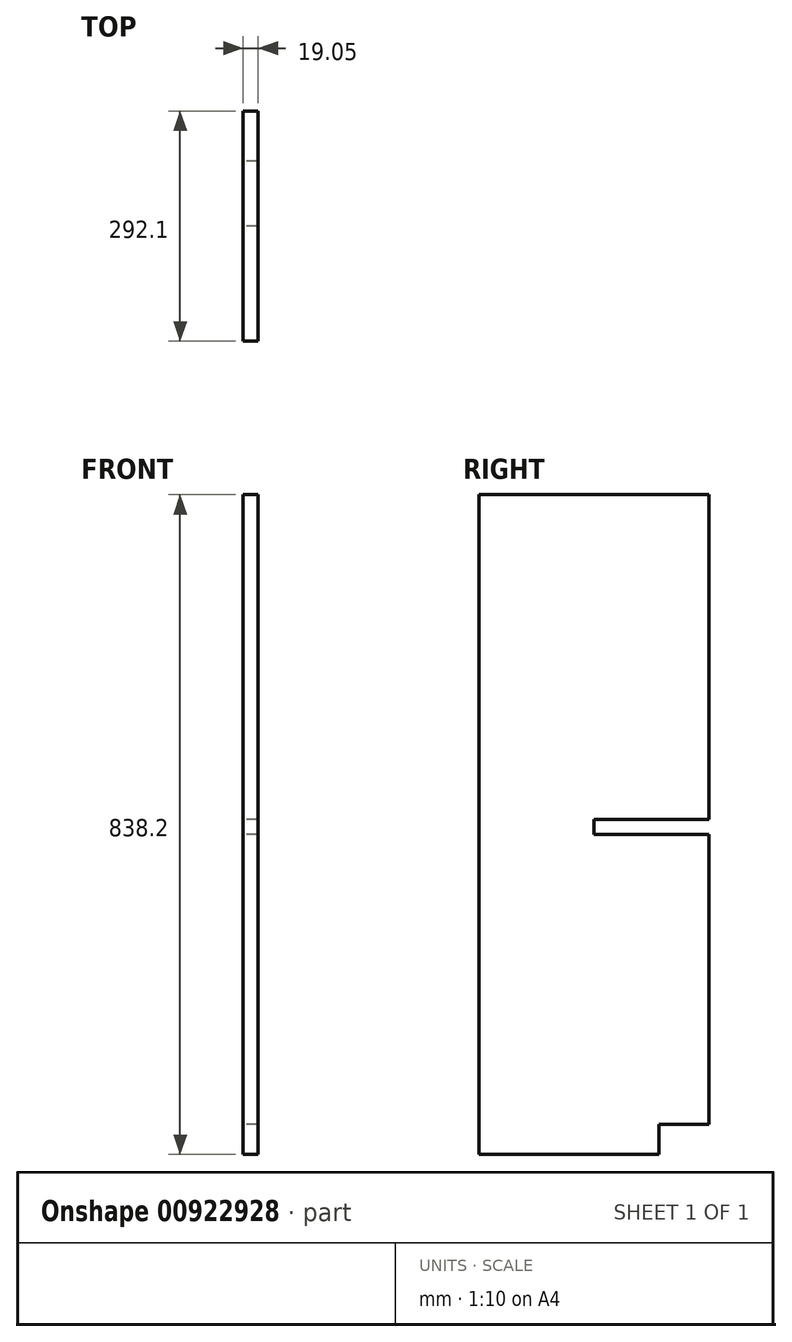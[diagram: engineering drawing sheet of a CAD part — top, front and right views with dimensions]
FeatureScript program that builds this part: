
annotation { "Feature Type Name" : "Feature", "Feature Type Description" : "" }
export const myFeature = defineFeature(function(context is Context, id is Id, definition is map)
    precondition{}
    {
        {
            var Q0;
            Q0=qCreatedBy(makeId("Right.planeOp"),FACE);
            var sketch = newSketch(context, id + "F0", { "sketchPlane" : qUnion([Q0])});
            skLineSegment(sketch, "E0.bottom", {"start": v(-146.05, 419.1) * mm, "end": v(146.05, 419.1) * mm});
            skLineSegment(sketch, "E0.top", {"start": v(-146.05, -419.1) * mm, "end": v(146.05, -419.1) * mm});
            skLineSegment(sketch, "E0.left", {"start": v(-146.05, 419.1) * mm, "end": v(-146.05, -419.1) * mm});
            skLineSegment(sketch, "E0.right", {"start": v(146.05, 419.1) * mm, "end": v(146.05, -419.1) * mm});
            skPoint(sketch, "E0.middle", {"position": v(0, 0) * mm});
            skLineSegment(sketch, "E1.bottom", {"start": v(146.05, -419.1) * mm, "end": v(82.55, -419.1) * mm});
            skLineSegment(sketch, "E1.top", {"start": v(146.05, -381) * mm, "end": v(82.55, -381) * mm});
            skLineSegment(sketch, "E1.left", {"start": v(146.05, -419.1) * mm, "end": v(146.05, -381) * mm});
            skLineSegment(sketch, "E1.right", {"start": v(82.55, -419.1) * mm, "end": v(82.55, -381) * mm});
            skLineSegment(sketch, "E2.0", {"start": v(-146.05, -12.7) * mm, "end": v(184.15, -12.7) * mm});
            skLineSegment(sketch, "E3.0", {"start": v(-146.05, 6.35) * mm, "end": v(184.15, 6.35) * mm});
            skLineSegment(sketch, "E4", {"start": v(0, -419.1) * mm, "end": v(0, 419.1) * mm});
            skSolve(sketch);
        }
        {
            var Q0;
            {var subQ0=sQuery(id+"F0.wireOp",EDGE,"E0.left");var subQ1=sQuery(id+"F0.wireOp",EDGE,"E0.bottom");var subQ2=makeQuery(id+"F0.imprint","INTERSECT",VERTEX,{"derivedFrom":[subQ1,subQ0]});Q0=makeQuery(id+"F0.imprint","IMPRINT",FACE,{"disambiguationData":[TD([[makeQuery(id+"F0.imprint","IMPRINT",EDGE,{"disambiguationData":[TD([[subQ2,-1.0]])],"derivedFrom":subQ1}),-1.0]])]});}
            var Q1;
            {var subQ0=sQuery(id+"F0.wireOp",EDGE,"E0.right");var subQ1=sQuery(id+"F0.wireOp",EDGE,"E0.bottom");var subQ2=makeQuery(id+"F0.imprint","INTERSECT",VERTEX,{"derivedFrom":[subQ1,subQ0]});Q1=makeQuery(id+"F0.imprint","IMPRINT",FACE,{"disambiguationData":[TD([[makeQuery(id+"F0.imprint","IMPRINT",EDGE,{"disambiguationData":[TD([[subQ2,1.0]])],"derivedFrom":subQ1}),-1.0]])]});}
            var Q2;
            {var subQ0=sQuery(id+"F0.wireOp",EDGE,"E1.top");Q2=makeQuery(id+"F0.imprint","IMPRINT",FACE,{"disambiguationData":[TD([[makeQuery(id+"F0.imprint","IMPRINT",EDGE,{"derivedFrom":subQ0}),-1.0]])]});}
            var Q3;
            {var subQ0=sQuery(id+"F0.wireOp",EDGE,"E0.left");var subQ1=sQuery(id+"F0.wireOp",EDGE,"E0.top");var subQ2=makeQuery(id+"F0.imprint","INTERSECT",VERTEX,{"derivedFrom":[subQ1,subQ0]});Q3=makeQuery(id+"F0.imprint","IMPRINT",FACE,{"disambiguationData":[TD([[makeQuery(id+"F0.imprint","IMPRINT",EDGE,{"disambiguationData":[TD([[subQ2,-1.0]])],"derivedFrom":subQ1}),1.0]])]});}
            var Q4;
            {var subQ0=sQuery(id+"F0.wireOp",EDGE,"E2.0");var subQ1=sQuery(id+"F0.wireOp",EDGE,"E0.left");var subQ2=makeQuery(id+"F0.imprint","INTERSECT",VERTEX,{"derivedFrom":[subQ1,subQ0]});Q4=makeQuery(id+"F0.imprint","IMPRINT",FACE,{"disambiguationData":[TD([[makeQuery(id+"F0.imprint","IMPRINT",EDGE,{"disambiguationData":[TD([[subQ2,1.0]])],"derivedFrom":subQ1}),1.0]])]});}
            extrude(context, id + "F1", {"entities" : qUnion([Q0, Q1, Q2, Q3, Q4]), "depth" : 19.05 * mm, "offsetDistance" : 25.4 * mm});
        }
    });
